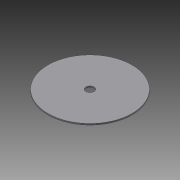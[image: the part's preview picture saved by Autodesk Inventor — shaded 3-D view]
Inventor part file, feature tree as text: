
AUTODESK INVENTOR PART (.ipt)
format: ipt  version: 2015 (Build 190159000, 159)  size: 72,192 bytes
history: native  units: mm
features: extrude x1, sketch x1
ambient origin geometry x8: Origin, YZ Plane, XZ Plane, XY Plane, X Axis, Y Axis, Z Axis, Center Point
bodies: Solid1 (feature_tree)
feature tree (2):
  extrude  "Extrusion1"  Depth=1.5mm
  sketch  "Sketch1"  dims[d0=9.18mm d1=94.0mm d2=1.5mm d3=0.0mm]
